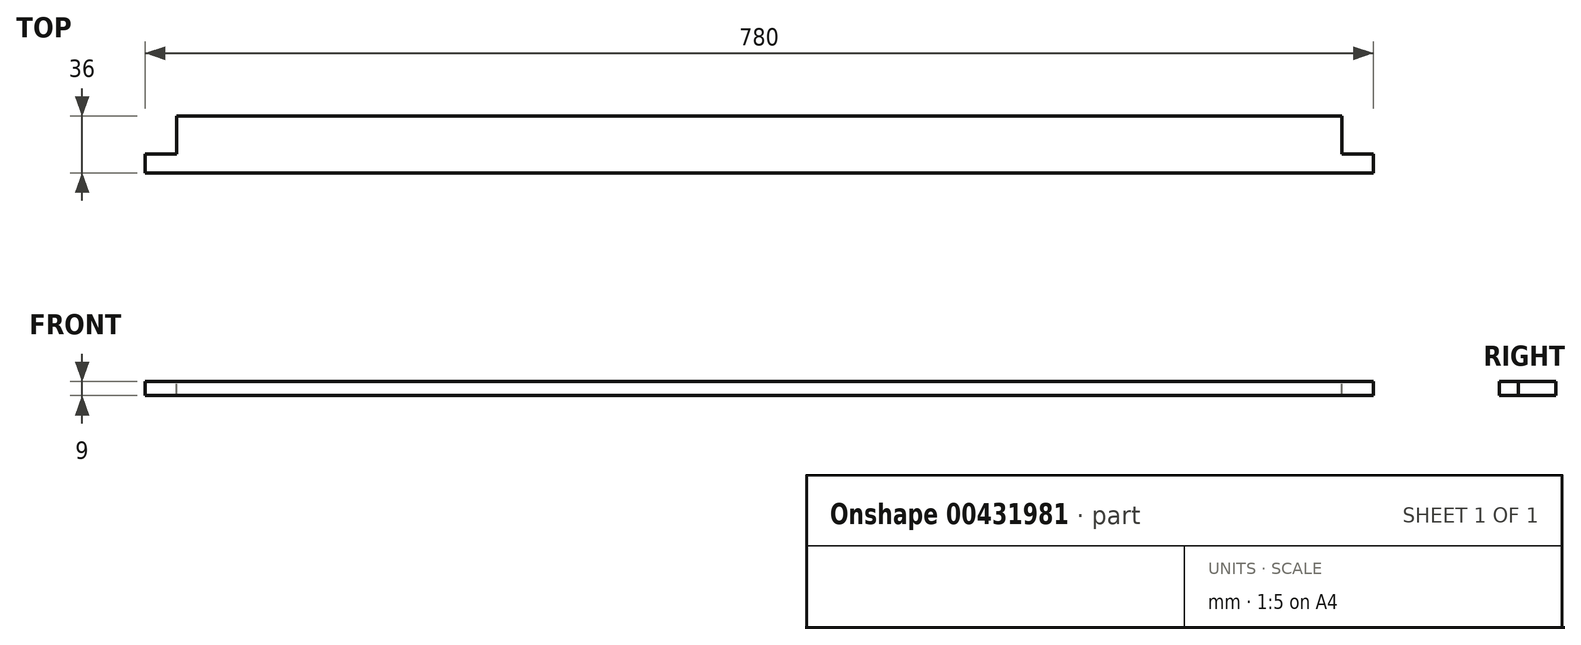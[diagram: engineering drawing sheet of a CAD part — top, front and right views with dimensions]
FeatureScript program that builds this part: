
annotation { "Feature Type Name" : "Feature", "Feature Type Description" : "" }
export const myFeature = defineFeature(function(context is Context, id is Id, definition is map)
    precondition{}
    {
        {
            var Q0;
            Q0=qCreatedBy(makeId("Top.planeOp"),FACE);
            var sketch = newSketch(context, id + "F0", { "sketchPlane" : qUnion([Q0])});
            skLineSegment(sketch, "E0.bottom", {"start": v(-390, 18) * mm, "end": v(390, 18) * mm});
            skLineSegment(sketch, "E0.top", {"start": v(-390, -18) * mm, "end": v(390, -18) * mm});
            skLineSegment(sketch, "E0.left", {"start": v(-390, 18) * mm, "end": v(-390, -18) * mm});
            skLineSegment(sketch, "E0.right", {"start": v(390, 18) * mm, "end": v(390, -18) * mm});
            skPoint(sketch, "E0.middle", {"position": v(0, 0) * mm});
            skSolve(sketch);
        }
        {
            var Q0;
            Q0=qSketchRegion(id+"F0",true);
            extrude(context, id + "F1", {"entities" : qUnion([Q0]), "depth" : 9 * mm, "offsetDistance" : 25 * mm});
        }
        {
            var Q0;
            Q0=makeQuery(id+"F1.opExtrude","CAP_FACE",FACE,{"disambiguationData":[OSD([sQuery(id+"F0.wireOp",EDGE,"E0.bottom"),sQuery(id+"F0.wireOp",EDGE,"E0.top"),sQuery(id+"F0.wireOp",EDGE,"E0.left"),sQuery(id+"F0.wireOp",EDGE,"E0.right")])],"isStart":false});
            var sketch = newSketch(context, id + "F2", { "sketchPlane" : qUnion([Q0])});
            skLineSegment(sketch, "E1.bottom", {"start": v(-390, 18) * mm, "end": v(-370, 18) * mm});
            skLineSegment(sketch, "E1.top", {"start": v(-390, -6) * mm, "end": v(-370, -6) * mm});
            skLineSegment(sketch, "E1.left", {"start": v(-390, 18) * mm, "end": v(-390, -6) * mm});
            skLineSegment(sketch, "E1.right", {"start": v(-370, 18) * mm, "end": v(-370, -6) * mm});
            skLineSegment(sketch, "E2.bottom", {"start": v(370, 18) * mm, "end": v(390, 18) * mm});
            skLineSegment(sketch, "E2.top", {"start": v(370, -6) * mm, "end": v(390, -6) * mm});
            skLineSegment(sketch, "E2.left", {"start": v(370, 18) * mm, "end": v(370, -6) * mm});
            skLineSegment(sketch, "E2.right", {"start": v(390, 18) * mm, "end": v(390, -6) * mm});
            skSolve(sketch);
        }
        {
            var Q0;
            Q0=qSketchRegion(id+"F2",true);
            extrude(context, id + "F3", {"entities" : qUnion([Q0]), "operationType" : NewBodyOperationType.REMOVE, "endBound" : BoundingType.UP_TO_NEXT, "oppositeDirection" : true, "depth" : 25 * mm});
        }
    });
